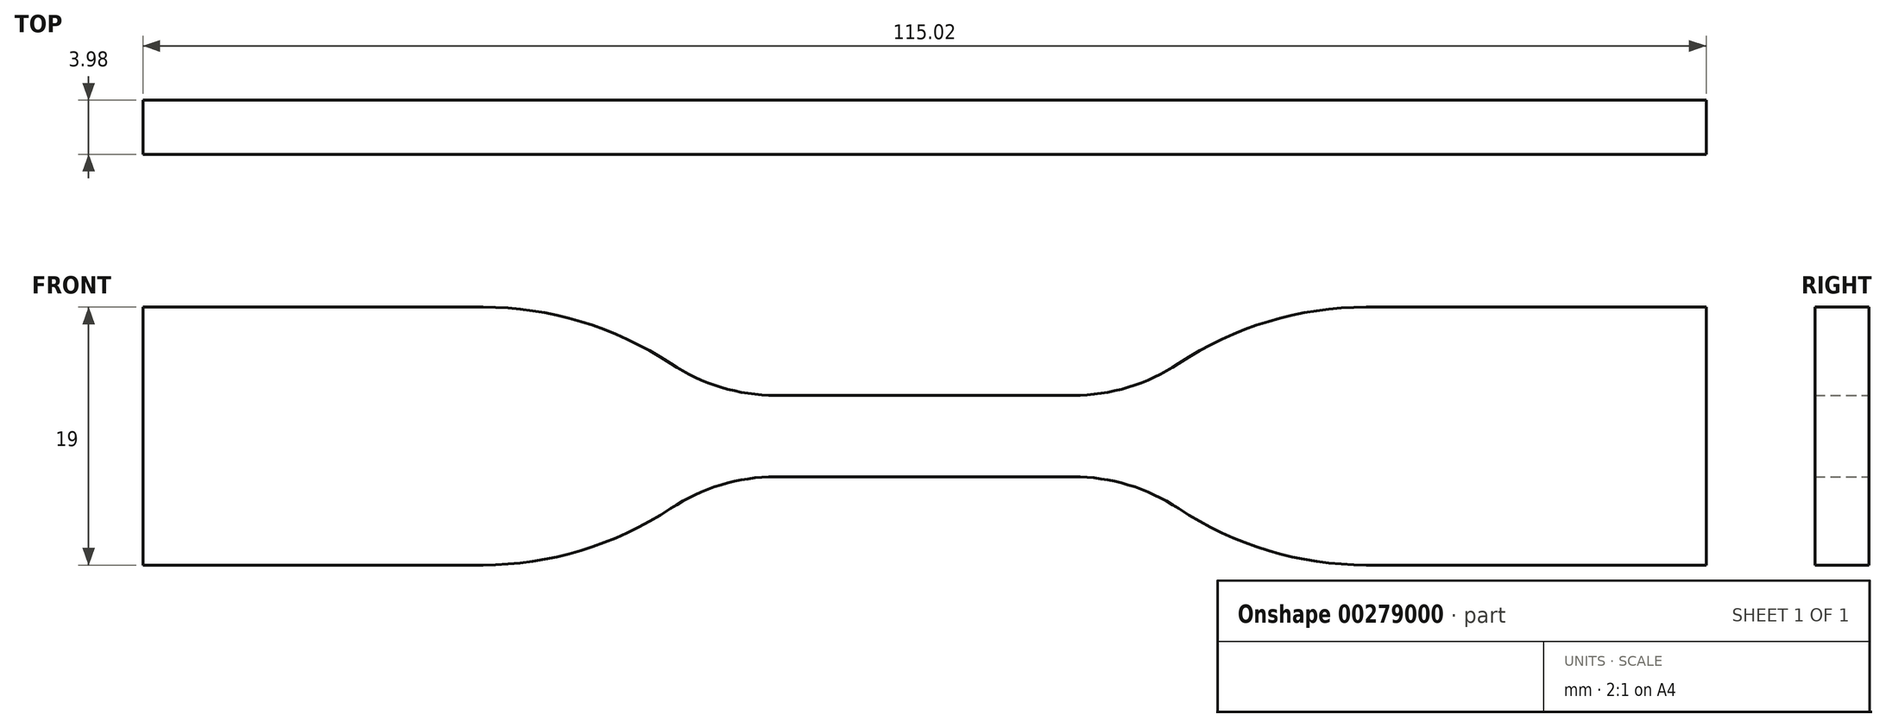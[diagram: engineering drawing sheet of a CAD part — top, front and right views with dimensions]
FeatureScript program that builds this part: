
annotation { "Feature Type Name" : "Feature", "Feature Type Description" : "" }
export const myFeature = defineFeature(function(context is Context, id is Id, definition is map)
    precondition{}
    {
        {
            var Q0;
            Q0=qCreatedBy(makeId("Front.planeOp"),FACE);
            var sketch = newSketch(context, id + "F0", { "sketchPlane" : qUnion([Q0])});
            skLineSegment(sketch, "E0.MirrorCS", {"start": v(0, 3) * mm, "end": v(-10.94, 3) * mm});
            skArc(sketch, "E1", {"start": v(-18.68, 5.33) * mm, "mid": v(-14.98, 3.6) * mm, "end": v(-10.94, 3) * mm});
            skArc(sketch, "E2", {"start": v(-18.68, 5.33) * mm, "mid": v(-25.28, 8.43) * mm, "end": v(-32.5, 9.5) * mm});
            skLineSegment(sketch, "E3", {"start": v(-57.5, 9.5) * mm, "end": v(-32.5, 9.5) * mm});
            skLineSegment(sketch, "E4.MirrorCS", {"start": v(0, 3) * mm, "end": v(10.94, 3) * mm});
            skLineSegment(sketch, "E5.MirrorCS", {"start": v(57.5, 9.5) * mm, "end": v(32.5, 9.5) * mm});
            skArc(sketch, "E6.MirrorCS", {"start": v(18.68, 5.33) * mm, "mid": v(14.98, 3.6) * mm, "end": v(10.94, 3) * mm});
            skArc(sketch, "E7.MirrorCS", {"start": v(18.68, 5.33) * mm, "mid": v(25.28, 8.43) * mm, "end": v(32.5, 9.5) * mm});
            skLineSegment(sketch, "E8.MirrorCS", {"start": v(0, -3) * mm, "end": v(-10.94, -3) * mm});
            skLineSegment(sketch, "E9.MirrorCS", {"start": v(0, -3) * mm, "end": v(10.94, -3) * mm});
            skLineSegment(sketch, "E10.MirrorCS", {"start": v(57.5, -9.5) * mm, "end": v(32.5, -9.5) * mm});
            skArc(sketch, "E11.MirrorCS", {"start": v(18.68, -5.33) * mm, "mid": v(25.28, -8.43) * mm, "end": v(32.5, -9.5) * mm});
            skArc(sketch, "E12.MirrorCS", {"start": v(-18.68, -5.33) * mm, "mid": v(-25.28, -8.43) * mm, "end": v(-32.5, -9.5) * mm});
            skLineSegment(sketch, "E13.MirrorCS", {"start": v(-57.5, -9.5) * mm, "end": v(-32.5, -9.5) * mm});
            skArc(sketch, "E14.MirrorCS", {"start": v(-18.68, -5.33) * mm, "mid": v(-14.98, -3.6) * mm, "end": v(-10.94, -3) * mm});
            skArc(sketch, "E15.MirrorCS", {"start": v(18.68, -5.33) * mm, "mid": v(14.98, -3.6) * mm, "end": v(10.94, -3) * mm});
            skLineSegment(sketch, "E16", {"start": v(-57.5, 9.5) * mm, "end": v(-57.5, -9.5) * mm});
            skLineSegment(sketch, "E17", {"start": v(57.5, 9.5) * mm, "end": v(57.5, -9.5) * mm});
            skSolve(sketch);
        }
        {
            var Q0;
            Q0=makeQuery(id+"F0.imprint","IMPRINT",FACE,{"disambiguationData":[TD([[makeQuery(id+"F0.imprint","IMPRINT",EDGE,{"derivedFrom":sQuery(id+"F0.wireOp",EDGE,"E0.MirrorCS")}),1.0]])]});
            extrude(context, id + "F1", {"entities" : qUnion([Q0]), "endBound" : BoundingType.SYMMETRIC, "depth" : 4 * mm});
        }
    });
